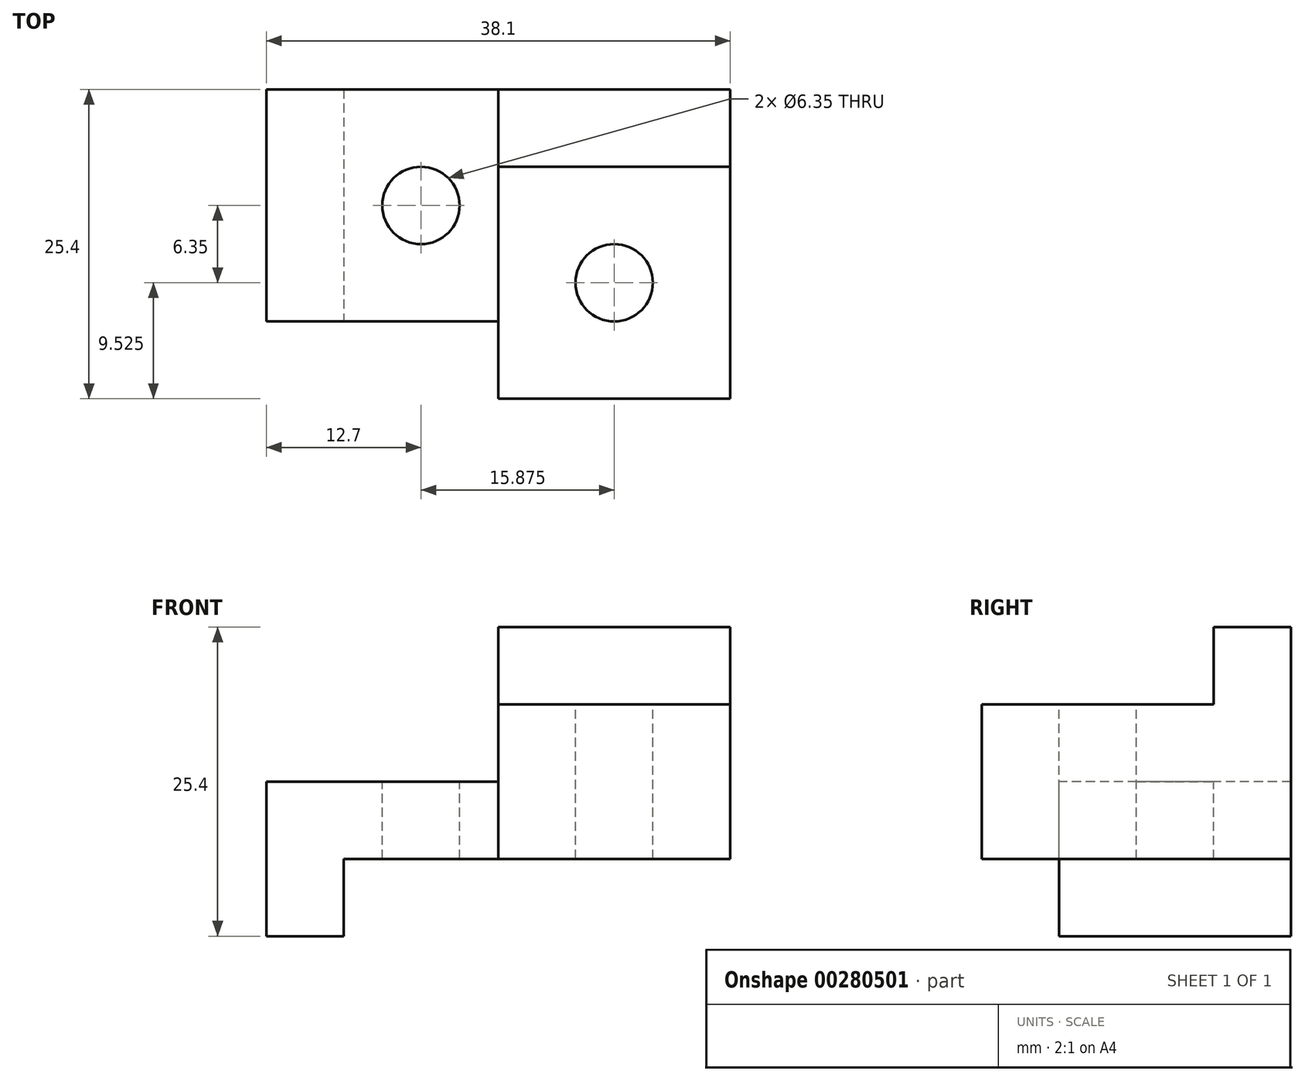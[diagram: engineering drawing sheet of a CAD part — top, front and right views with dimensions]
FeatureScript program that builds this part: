
annotation { "Feature Type Name" : "Feature", "Feature Type Description" : "" }
export const myFeature = defineFeature(function(context is Context, id is Id, definition is map)
    precondition{}
    {
        {
            var Q0;
            Q0=qCreatedBy(makeId("Top.planeOp"),FACE);
            var sketch = newSketch(context, id + "F0", { "sketchPlane" : qUnion([Q0])});
            skLineSegment(sketch, "E0", {"start": v(0, 0) * mm, "end": v(0, -6.35) * mm});
            skLineSegment(sketch, "E1", {"start": v(0, -6.35) * mm, "end": v(19.05, -6.35) * mm});
            skLineSegment(sketch, "E2", {"start": v(19.05, -6.35) * mm, "end": v(19.05, 19.05) * mm});
            skLineSegment(sketch, "E3", {"start": v(19.05, 19.05) * mm, "end": v(0, 19.05) * mm});
            skLineSegment(sketch, "E4", {"start": v(0, 19.05) * mm, "end": v(-19.05, 19.05) * mm});
            skLineSegment(sketch, "E5", {"start": v(-19.05, 19.05) * mm, "end": v(-19.05, 0) * mm});
            skLineSegment(sketch, "E6", {"start": v(-19.05, 0) * mm, "end": v(0, 0) * mm});
            skLineSegment(sketch, "E7", {"start": v(0, 19.05) * mm, "end": v(0, 12.7) * mm});
            skLineSegment(sketch, "E8", {"start": v(0, 12.7) * mm, "end": v(19.05, 12.7) * mm});
            skLineSegment(sketch, "E9", {"start": v(0, 12.7) * mm, "end": v(0, 0) * mm});
            skCircle(sketch, "E10", {"center": v(9.53, 3.18) * mm, "radius": 3.18 * mm});
            skCircle(sketch, "E11", {"center": v(-6.35, 9.53) * mm, "radius": 3.18 * mm});
            skLineSegment(sketch, "E12", {"start": v(-12.7, 19.05) * mm, "end": v(-12.7, 0) * mm});
            skSolve(sketch);
        }
        {
            var Q0;
            {var subQ1=sQuery(id+"F0.wireOp",EDGE,"E7");Q0=makeQuery(id+"F0.imprint","IMPRINT",FACE,{"disambiguationData":[TD([[makeQuery(id+"F0.imprint","IMPRINT",EDGE,{"derivedFrom":subQ1}),-1.0]])]});}
            var Q1;
            {var subQ0=sQuery(id+"F0.wireOp",EDGE,"E3");Q1=makeQuery(id+"F0.imprint","IMPRINT",FACE,{"disambiguationData":[TD([[makeQuery(id+"F0.imprint","IMPRINT",EDGE,{"derivedFrom":subQ0}),1.0]])]});}
            var Q2;
            Q2=makeQuery(id+"F0.imprint","IMPRINT",FACE,{"disambiguationData":[TD([[makeQuery(id+"F0.imprint","IMPRINT",EDGE,{"derivedFrom":sQuery(id+"F0.wireOp",EDGE,"E0")}),1.0]])]});
            extrude(context, id + "F1", {"entities" : qUnion([Q0, Q1, Q2]), "oppositeDirection" : true, "depth" : 6.35 * mm});
        }
        {
            var Q0;
            {var subQ0=sQuery(id+"F0.wireOp",EDGE,"E5");Q0=makeQuery(id+"F0.imprint","IMPRINT",FACE,{"disambiguationData":[TD([[makeQuery(id+"F0.imprint","IMPRINT",EDGE,{"derivedFrom":subQ0}),1.0]])]});}
            extrude(context, id + "F2", {"entities" : qUnion([Q0]), "operationType" : NewBodyOperationType.ADD, "oppositeDirection" : true, "depth" : 12.7 * mm});
        }
        {
            var Q0;
            Q0=makeQuery(id+"F0.imprint","IMPRINT",FACE,{"disambiguationData":[TD([[makeQuery(id+"F0.imprint","IMPRINT",EDGE,{"derivedFrom":sQuery(id+"F0.wireOp",EDGE,"E0")}),1.0]])]});
            extrude(context, id + "F3", {"entities" : qUnion([Q0]), "operationType" : NewBodyOperationType.ADD, "depth" : 6.35 * mm});
        }
        {
            var Q0;
            {var subQ0=sQuery(id+"F0.wireOp",EDGE,"E3");Q0=makeQuery(id+"F0.imprint","IMPRINT",FACE,{"disambiguationData":[TD([[makeQuery(id+"F0.imprint","IMPRINT",EDGE,{"derivedFrom":subQ0}),1.0]])]});}
            extrude(context, id + "F4", {"entities" : qUnion([Q0]), "operationType" : NewBodyOperationType.ADD, "depth" : 12.7 * mm});
        }
    });
